# Revit family: Electrical_Controls_Conspec_Optio-XP-Wireless-Gas-Detector
name_source: partatom
category: Electrical Fixtures
units: mm (PartAtom-declared; Revit-internal decimal feet)

## family parameters
Classification Number = 23.85.30.21
Cut with Voids When Loaded = No
Host = Face
Maintain Annotation Orientation = No
Part Type = Normal
Room Calculation Point = No
Round Connector Dimension = Use Diameter
Shared = No

## types (3) — shared parameters
Alarm = 4 Custom Alarm Levels with hysteresis and hold-to-alarm times, sensor Fail-High and Fail-Low alarms
Assembly Code = D5030
Battery Life = Up to 1 year
Date Updated = 2023/10/17
Depth = 5.09 "
Display = Intuitive menu using graphical LCD
Feature = Up to 6 sensors with capability to detect over 100 gases
Height = 7.5 "
Keynote = 16000
Manufacturer = CONSPEC Controls
Note = 32 Wireless Detectors per Gateway
Operating Humidity = 0% to 99% RH Non-Condesing
Operating Temperature = -4°F to +140°F
Power Source = Battery powered
Product Material = Conspec - Metal - Steel - Powder Coated - Blue
Product data url = https://bimobject.com
Sensor Extension = Up to 100ft
Sensory Types = 3 Plug-and-Play Electrochemical sensors and 3 NDIR sensors
URL = https://www.conspec-controls.com
Version = 1
Weight = 9.00 lbf
Width = 5.71 "
zero-valued in all types: Default Elevation

## per-type parameters (varying)
| type | Description | Model | z_Sensor 1 | z_Sensor 2 |
| OPTIO XP Wireless Single Gas | OPTIO XP Wireless Single Gas Detector | OPTIO XP Wireless Single Gas Detector | Yes | No |
| OPTIO XP Wireless Multi Gas | OPTIO XP Wireless Multi Gas Detector | OPTIO XP Wireless Multi Gas Detector | Yes | Yes |
| OPTIO XP Wireless Gateway | OPTIO XP Wireless Gateway | OPTIO XP Wireless Gateway | No | No |

## geometry (parser evidence)
native form markers: Sweep x1
no freeform markers — native parametric forms only
